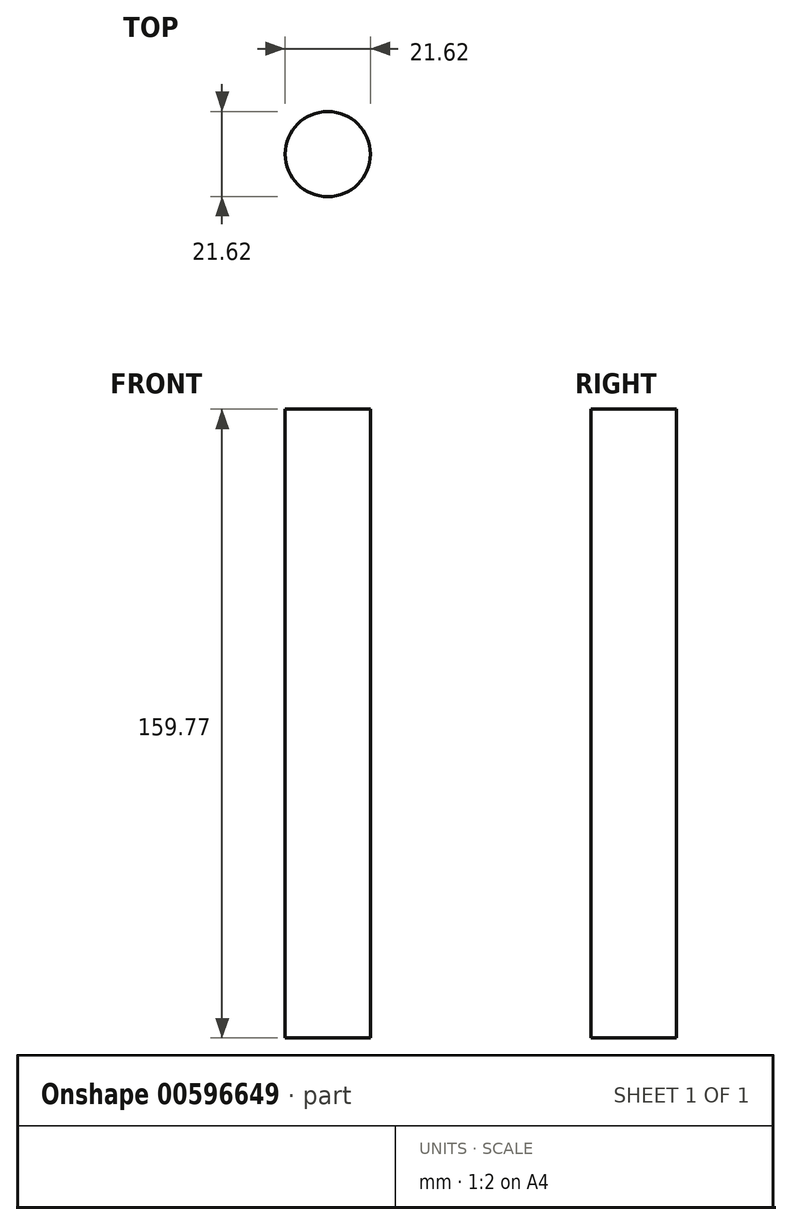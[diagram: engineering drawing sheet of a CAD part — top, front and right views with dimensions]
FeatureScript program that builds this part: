
annotation { "Feature Type Name" : "Feature", "Feature Type Description" : "" }
export const myFeature = defineFeature(function(context is Context, id is Id, definition is map)
    precondition{}
    {
        {
            var Q0;
            Q0=qCreatedBy(makeId("Top.planeOp"),FACE);
            var sketch = newSketch(context, id + "F0", { "sketchPlane" : qUnion([Q0])});
            skCircle(sketch, "E0", {"center": v(0, 0) * mm, "radius": 10.81 * mm});
            skSolve(sketch);
        }
        {
            var Q0;
            Q0 = qSketchRegion(id + "F0", true);
            extrude(context, id + "F1", {"entities" : qUnion([Q0]), "depth" : 159.77 * mm, "offsetDistance" : 25.4 * mm});
        }
    });
